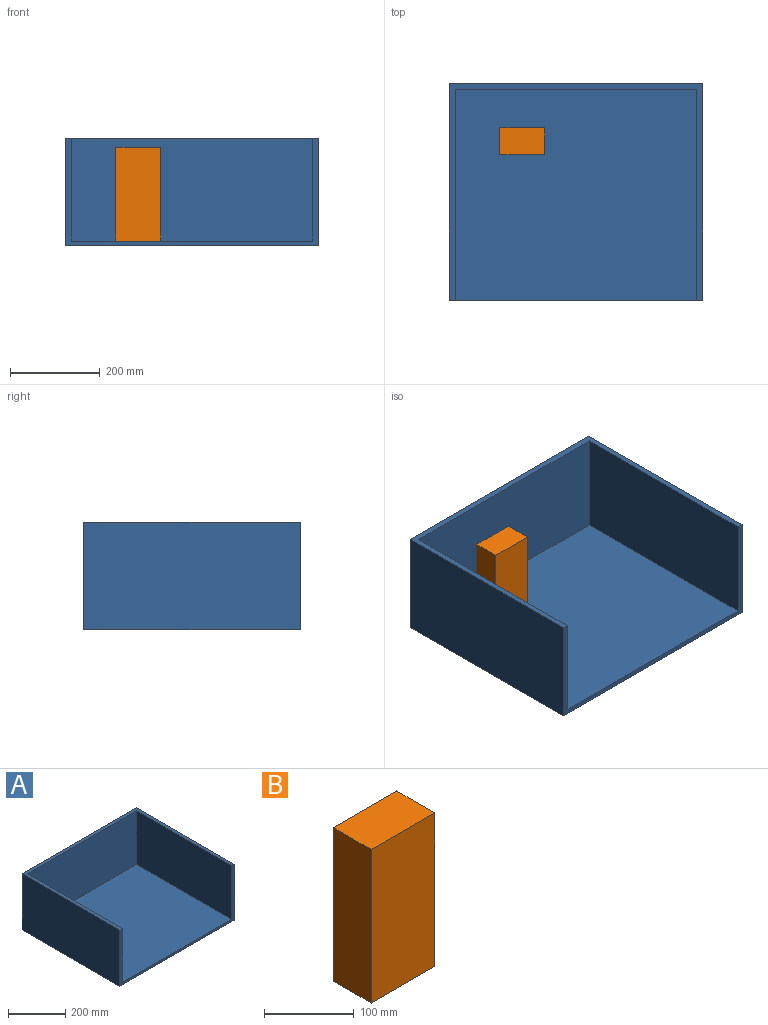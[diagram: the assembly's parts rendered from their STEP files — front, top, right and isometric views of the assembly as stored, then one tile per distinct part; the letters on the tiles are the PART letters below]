
ASSEMBLY  parts=2 mates=1
PART A: 10 faces, bbox 565x483.5x241 mm
  f0: plane 565x483.5mm, normal (0,0,1), area 19377.5mm2, adj f1,f2,f3,f4,f5,f6,f9
  f1: plane 565x241mm, normal (0,-1,0), area 11965mm2, adj f0,f2,f3,f5,f6,f7,f8
  f2: plane 483.5x241mm, normal (-1,0,0), area 116523.5mm2, adj f0,f1,f8,f9
  f3: plane 470x230mm, normal (1,0,0), area 108100mm2, adj f0,f1,f4,f7
  f4: plane 540x230mm, normal (0,-1,0), area 124200mm2, adj f0,f3,f6,f7
  f5: plane 483.5x241mm, normal (1,0,0), area 116523.5mm2, adj f0,f1,f8,f9
  f6: plane 470x230mm, normal (-1,0,0), area 108100mm2, adj f0,f1,f4,f7
  f7: plane 540x470mm, normal (0,0,1), area 253800mm2, adj f1,f3,f4,f6
  f8: plane 565x483.5mm, normal (0,0,-1), area 273177.5mm2, adj f1,f2,f5,f9
  f9: plane 565x241mm, normal (0,1,0), area 136165mm2, adj f0,f2,f5,f8
PART B: 6 faces, bbox 100x59.8x209.3 mm
  f0: plane 209.27x100mm, normal (0,-1,0), area 20927mm2, adj f1,f3,f4,f5
  f1: plane 209.27x59.8mm, normal (1,0,0), area 12514.3mm2, adj f0,f2,f4,f5
  f2: plane 209.27x100mm, normal (0,1,0), area 20927mm2, adj f1,f3,f4,f5
  f3: plane 209.27x59.8mm, normal (-1,0,0), area 12514.3mm2, adj f0,f2,f4,f5
  f4: plane 100x59.8mm, normal (0,0,1), area 5980mm2, adj f0,f1,f2,f3
  f5: plane 100x59.8mm, normal (0,0,-1), area 5980mm2, adj f0,f1,f2,f3
PLACE A t=(-92.68,71.55,209.32)mm
PLACE B t=(412.69,96.34,209.32)mm
MATE fastened B.f5 <-> A.f7  axis (0,0,-1) through (2.57,3.71,209.32)mm
